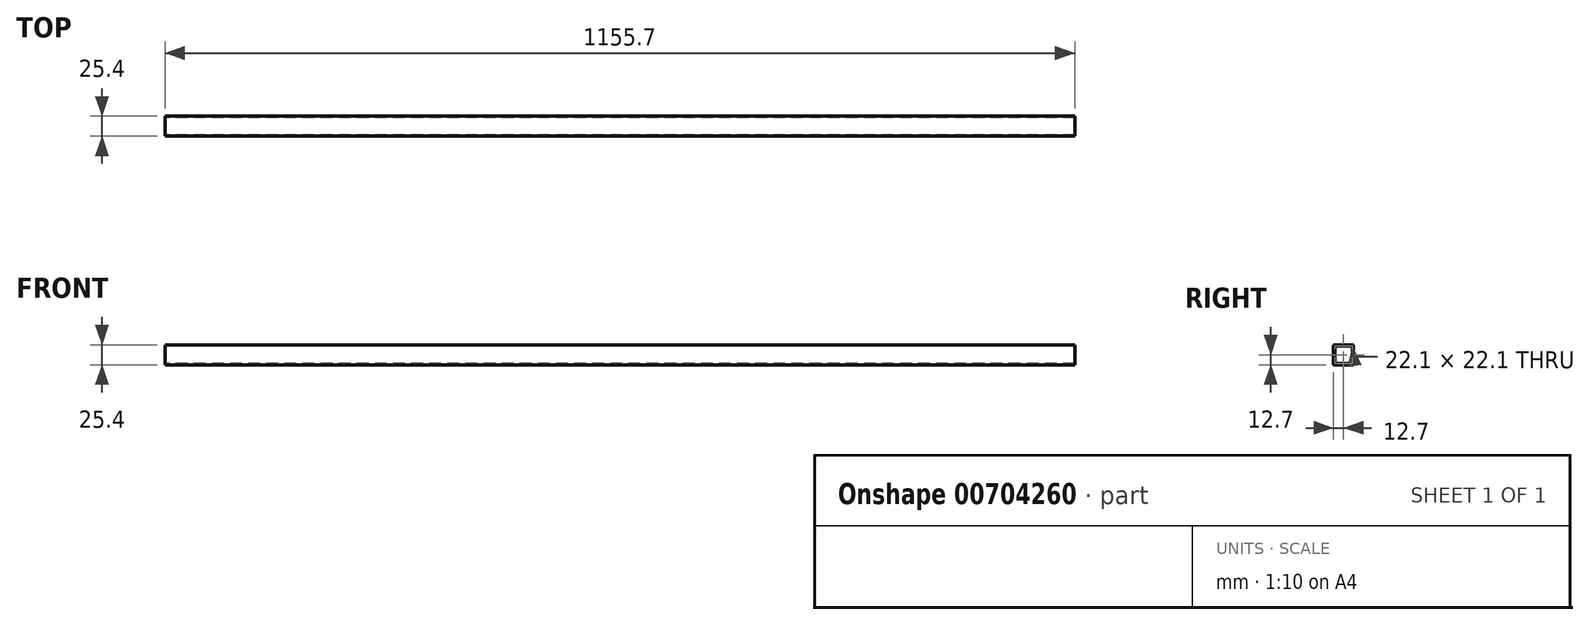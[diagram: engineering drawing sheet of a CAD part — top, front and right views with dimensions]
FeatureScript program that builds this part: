
annotation { "Feature Type Name" : "Feature", "Feature Type Description" : "" }
export const myFeature = defineFeature(function(context is Context, id is Id, definition is map)
    precondition{}
    {
        {
            var Q0;
            Q0=qCreatedBy(makeId("Front.planeOp"),FACE);
            var sketch = newSketch(context, id + "F0", { "sketchPlane" : qUnion([Q0])});
            skLineSegment(sketch, "E0.bottom", {"start": v(-577.85, 12.7) * mm, "end": v(577.85, 12.7) * mm});
            skLineSegment(sketch, "E0.top", {"start": v(-577.85, -12.7) * mm, "end": v(577.85, -12.7) * mm});
            skLineSegment(sketch, "E0.left", {"start": v(-577.85, 12.7) * mm, "end": v(-577.85, -12.7) * mm});
            skLineSegment(sketch, "E0.right", {"start": v(577.85, 12.7) * mm, "end": v(577.85, -12.7) * mm});
            skPoint(sketch, "E0.middle", {"position": v(0, 0) * mm});
            skSolve(sketch);
        }
        {
            var Q0;
            Q0=qCreatedBy(makeId("Right.planeOp"),FACE);
            var sketch = newSketch(context, id + "F1", { "sketchPlane" : qUnion([Q0])});
            skLineSegment(sketch, "E1.bottom", {"start": v(11.05, 11.05) * mm, "end": v(-11.05, 11.05) * mm});
            skLineSegment(sketch, "E1.top", {"start": v(11.05, -11.05) * mm, "end": v(-11.05, -11.05) * mm});
            skLineSegment(sketch, "E1.left", {"start": v(11.05, 11.05) * mm, "end": v(11.05, -11.05) * mm});
            skLineSegment(sketch, "E1.right", {"start": v(-11.05, 11.05) * mm, "end": v(-11.05, -11.05) * mm});
            skPoint(sketch, "E1.middle", {"position": v(0, 0) * mm});
            skSolve(sketch);
        }
        {
            var Q0;
            Q0=makeQuery(id+"F0.imprint","IMPRINT",FACE,{"disambiguationData":[TD([[makeQuery(id+"F0.imprint","IMPRINT",EDGE,{"derivedFrom":sQuery(id+"F0.wireOp",EDGE,"E0.bottom")}),-1.0]])]});
            extrude(context, id + "F2", {"entities" : qUnion([Q0]), "endBound" : BoundingType.SYMMETRIC, "depth" : 25.4 * mm, "offsetDistance" : 25.4 * mm});
        }
        {
            var Q0;
            Q0=makeQuery(id+"F1.imprint","IMPRINT",FACE,{"disambiguationData":[TD([[makeQuery(id+"F1.imprint","IMPRINT",EDGE,{"derivedFrom":sQuery(id+"F1.wireOp",EDGE,"E1.bottom")}),1.0]])]});
            extrude(context, id + "F3", {"entities" : qUnion([Q0]), "operationType" : NewBodyOperationType.REMOVE, "endBound" : BoundingType.SYMMETRIC, "depth" : 1155.7 * mm, "offsetDistance" : 25.4 * mm});
        }
    });
